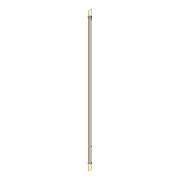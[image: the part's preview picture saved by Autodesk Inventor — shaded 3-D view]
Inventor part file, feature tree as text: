
AUTODESK INVENTOR PART (.ipt)
format: ipt  version: 2022 (Build 260153000, 153)  size: 107,520 bytes
history: native  units: mm
features: extrude x2, sketch x2
ambient origin geometry x8: Origin, YZ Plane, XZ Plane, XY Plane, X Axis, Y Axis, Z Axis, Center Point
bodies: Solid1 (feature_tree)
feature tree (4):
  extrude  "Extrusion1"  Depth=10.0mm
  extrude  "Extrusion2"  Depth=4.0mm
  sketch  "Sketch1"  dims[d0=12.0mm d1=10.0mm]
  sketch  "Sketch2"  dims[d2=500.0mm d3=0.0mm d4=3.0mm d5=3.0mm d6=4.0mm d8=320.0mm d9=0.0mm d10=3.0mm d11=6.5mm d12=55.0mm d13=0.872665mm d14=0.5mm d15=0.872665mm]
